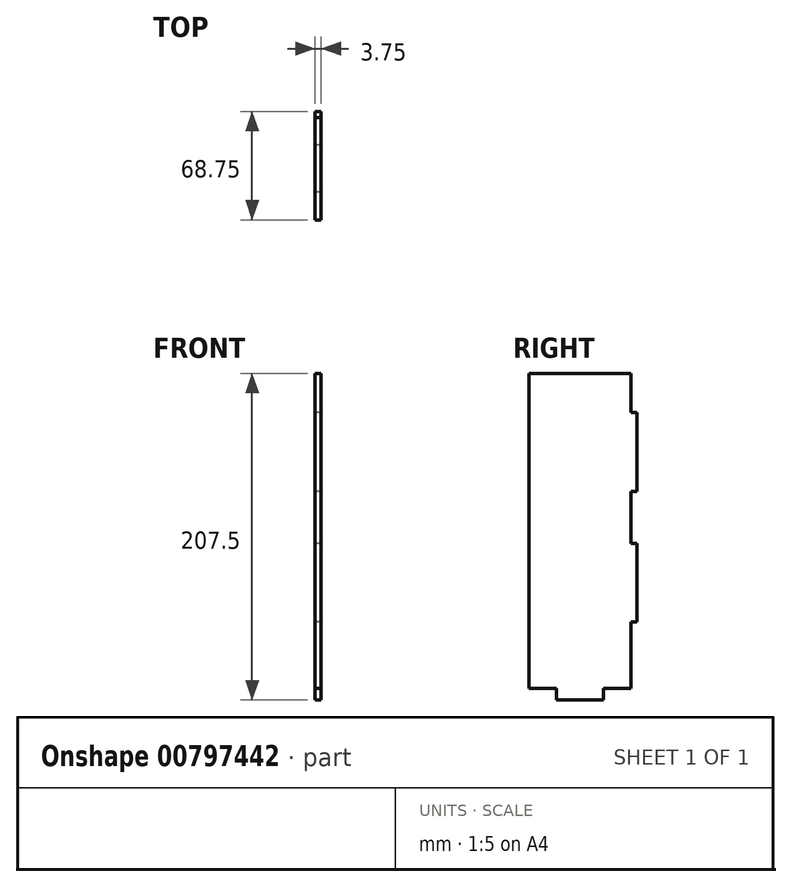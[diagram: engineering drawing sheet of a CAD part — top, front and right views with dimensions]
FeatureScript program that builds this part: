
annotation { "Feature Type Name" : "Feature", "Feature Type Description" : "" }
export const myFeature = defineFeature(function(context is Context, id is Id, definition is map)
    precondition{}
    {
        {
            var Q0;
            Q0=qCreatedBy(makeId("Right.planeOp"),FACE);
            var sketch = newSketch(context, id + "F0", { "sketchPlane" : qUnion([Q0])});
            skLineSegment(sketch, "E0.bottom", {"start": v(0, 8.05) * mm, "end": v(17.5, 8.05) * mm});
            skLineSegment(sketch, "E0.top", {"start": v(0, 208.05) * mm, "end": v(65, 208.05) * mm});
            skLineSegment(sketch, "E0.left", {"start": v(0, 8.05) * mm, "end": v(0, 208.05) * mm});
            skLineSegment(sketch, "E0.right", {"start": v(65, 8.05) * mm, "end": v(65, 50.05) * mm});
            skLineSegment(sketch, "E1.top", {"start": v(17.5, 0.55) * mm, "end": v(47.5, 0.55) * mm});
            skLineSegment(sketch, "E1.left", {"start": v(17.5, 8.05) * mm, "end": v(17.5, 0.55) * mm});
            skLineSegment(sketch, "E1.right", {"start": v(47.5, 8.05) * mm, "end": v(47.5, 0.55) * mm});
            skLineSegment(sketch, "E2", {"start": v(65, 8.05) * mm, "end": v(47.5, 8.05) * mm});
            skLineSegment(sketch, "E3.bottom", {"start": v(65, 183.05) * mm, "end": v(68.75, 183.05) * mm});
            skLineSegment(sketch, "E3.top", {"start": v(65, 133.05) * mm, "end": v(68.75, 133.05) * mm});
            skLineSegment(sketch, "E3.right", {"start": v(68.75, 183.05) * mm, "end": v(68.75, 133.05) * mm});
            skLineSegment(sketch, "E4.bottom", {"start": v(65, 100.05) * mm, "end": v(68.75, 100.05) * mm});
            skLineSegment(sketch, "E4.top", {"start": v(65, 50.05) * mm, "end": v(68.75, 50.05) * mm});
            skLineSegment(sketch, "E4.right", {"start": v(68.75, 100.05) * mm, "end": v(68.75, 50.05) * mm});
            skLineSegment(sketch, "E5.trimOffspring", {"start": v(65, 100.05) * mm, "end": v(65, 133.05) * mm});
            skLineSegment(sketch, "E6", {"start": v(65, 208.05) * mm, "end": v(65, 183.05) * mm});
            skSolve(sketch);
        }
        {
            var Q0;
            Q0=makeQuery(id+"F0.imprint","IMPRINT",FACE,{"disambiguationData":[TD([[makeQuery(id+"F0.imprint","IMPRINT",EDGE,{"derivedFrom":sQuery(id+"F0.wireOp",EDGE,"E0.bottom")}),1.0]])]});
            extrude(context, id + "F1", {"entities" : qUnion([Q0]), "depth" : 3.75 * mm, "offsetDistance" : 25 * mm});
        }
    });
